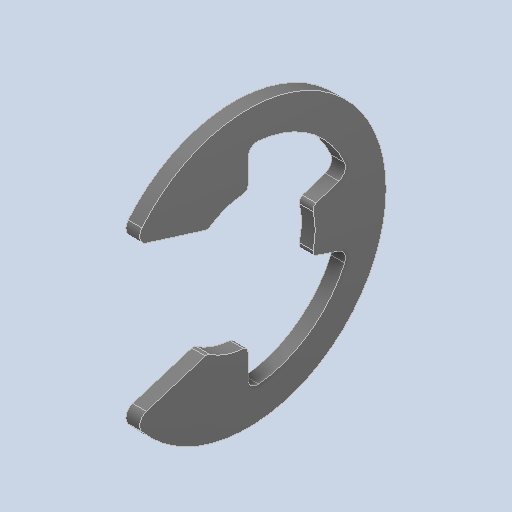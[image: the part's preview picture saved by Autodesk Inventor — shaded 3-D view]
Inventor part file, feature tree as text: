
AUTODESK INVENTOR PART (.ipt)
format: ipt  version: 2023.2 (Build 272271000, 271)  size: 116,736 bytes
history: native  units: in
note: dims shown in document units (in); Inventor stores cm internally (conversion verified against a paired STEP export)
features: fillet x1
ambient origin geometry x8: Origin, YZ Plane, XZ Plane, XY Plane, X Axis, Y Axis, Z Axis, Center Point
bodies: Solid1 (feature_tree)
feature tree (1):
  fillet  "Fillet2"  [1 undecoded]
note: 1 required parameter value undecoded (feature->parameter linkage not recoverable at this tier; creation-order binding heuristic only, values carry confidence <= 0.55)
